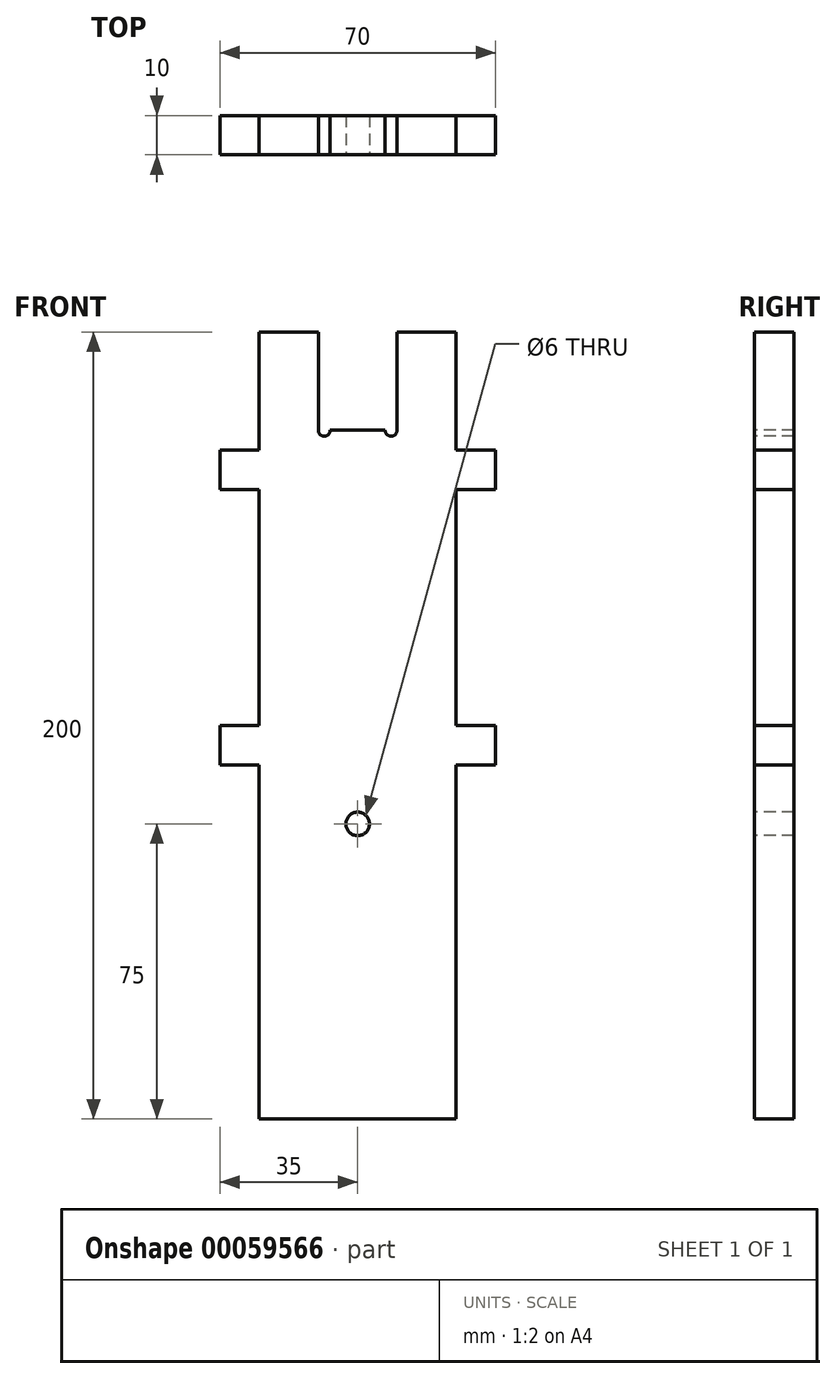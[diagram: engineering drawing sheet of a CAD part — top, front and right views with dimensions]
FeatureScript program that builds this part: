
annotation { "Feature Type Name" : "Feature", "Feature Type Description" : "" }
export const myFeature = defineFeature(function(context is Context, id is Id, definition is map)
    precondition{}
    {
        {
            var Q0;
            Q0=qCreatedBy(makeId("Front.planeOp"),FACE);
            var sketch = newSketch(context, id + "F0", { "sketchPlane" : qUnion([Q0])});
            skLineSegment(sketch, "E0.bottom", {"start": v(-25, 100) * mm, "end": v(25, 100) * mm});
            skLineSegment(sketch, "E0.top", {"start": v(-25, -100) * mm, "end": v(25, -100) * mm});
            skLineSegment(sketch, "E0.left", {"start": v(-25, 100) * mm, "end": v(-25, -100) * mm});
            skLineSegment(sketch, "E0.right", {"start": v(25, 100) * mm, "end": v(25, -100) * mm});
            skPoint(sketch, "E0.middle", {"position": v(0, 0) * mm});
            skSolve(sketch);
        }
        {
            var Q0;
            Q0=qSketchRegion(id+"F0",true);
            extrude(context, id + "F1", {"entities" : qUnion([Q0]), "depth" : 10 * mm});
        }
        {
            var Q0;
            Q0=makeQuery(id+"F1.opExtrude","CAP_FACE",FACE,{"disambiguationData":[OSD([sQuery(id+"F0.wireOp",EDGE,"E0.bottom"),sQuery(id+"F0.wireOp",EDGE,"E0.top"),sQuery(id+"F0.wireOp",EDGE,"E0.left"),sQuery(id+"F0.wireOp",EDGE,"E0.right")])],"isStart":false});
            var sketch = newSketch(context, id + "F2", { "sketchPlane" : qUnion([Q0])});
            skCircle(sketch, "E1", {"center": v(0, -25) * mm, "radius": 3 * mm});
            skSolve(sketch);
        }
        {
            var Q0;
            Q0=qSketchRegion(id+"F2",true);
            extrude(context, id + "F3", {"entities" : qUnion([Q0]), "operationType" : NewBodyOperationType.REMOVE, "oppositeDirection" : true, "depth" : 25 * mm});
        }
        {
            var Q0;
            Q0=makeQuery(id+"F1.opExtrude","CAP_FACE",FACE,{"disambiguationData":[OSD([sQuery(id+"F0.wireOp",EDGE,"E0.bottom"),sQuery(id+"F0.wireOp",EDGE,"E0.top"),sQuery(id+"F0.wireOp",EDGE,"E0.left"),sQuery(id+"F0.wireOp",EDGE,"E0.right")])],"isStart":false});
            var sketch = newSketch(context, id + "F4", { "sketchPlane" : qUnion([Q0])});
            skLineSegment(sketch, "E2.bottom", {"start": v(-10, 105) * mm, "end": v(10, 105) * mm});
            skLineSegment(sketch, "E2.top", {"start": v(-7, 75) * mm, "end": v(7, 75) * mm});
            skLineSegment(sketch, "E2.left", {"start": v(-10, 105) * mm, "end": v(-10, 75) * mm});
            skLineSegment(sketch, "E2.right", {"start": v(10, 105) * mm, "end": v(10, 75) * mm});
            skPoint(sketch, "E2.middle", {"position": v(0, 90) * mm});
            skArc(sketch, "E3", {"start": v(-10, 75) * mm, "mid": v(-8.5, 73.5) * mm, "end": v(-7, 75) * mm});
            skLineSegment(sketch, "E4", {"start": v(0, 75) * mm, "end": v(0, 25.67) * mm, "construction": true});
            skArc(sketch, "E5.MirrorCS", {"start": v(10, 75) * mm, "mid": v(8.5, 73.5) * mm, "end": v(7, 75) * mm});
            skSolve(sketch);
        }
        {
            var Q0;
            Q0=qSketchRegion(id+"F4",true);
            extrude(context, id + "F5", {"entities" : qUnion([Q0]), "operationType" : NewBodyOperationType.REMOVE, "oppositeDirection" : true, "depth" : 25 * mm});
        }
        {
            var Q0;
            Q0=makeQuery(id+"F1.opExtrude","CAP_FACE",FACE,{"disambiguationData":[OSD([sQuery(id+"F0.wireOp",EDGE,"E0.bottom"),sQuery(id+"F0.wireOp",EDGE,"E0.top"),sQuery(id+"F0.wireOp",EDGE,"E0.left"),sQuery(id+"F0.wireOp",EDGE,"E0.right")])],"isStart":false});
            var sketch = newSketch(context, id + "F6", { "sketchPlane" : qUnion([Q0])});
            skLineSegment(sketch, "E6.bottom", {"start": v(-25, 70) * mm, "end": v(-35, 70) * mm});
            skLineSegment(sketch, "E6.top", {"start": v(-25, 60) * mm, "end": v(-35, 60) * mm});
            skLineSegment(sketch, "E6.left", {"start": v(-25, 70) * mm, "end": v(-25, 60) * mm});
            skLineSegment(sketch, "E6.right", {"start": v(-35, 70) * mm, "end": v(-35, 60) * mm});
            skLineSegment(sketch, "E7.MirrorCS", {"start": v(25, 70) * mm, "end": v(35, 70) * mm});
            skLineSegment(sketch, "E8.MirrorCS", {"start": v(35, 70) * mm, "end": v(35, 60) * mm});
            skLineSegment(sketch, "E9.MirrorCS", {"start": v(25, 70) * mm, "end": v(25, 60) * mm});
            skLineSegment(sketch, "E10.MirrorCS", {"start": v(25, 60) * mm, "end": v(35, 60) * mm});
            skLineSegment(sketch, "E11", {"start": v(-25, 30) * mm, "end": v(25, 30) * mm, "construction": true});
            skLineSegment(sketch, "E12.MirrorCS", {"start": v(-25, -10) * mm, "end": v(-35, -10) * mm});
            skLineSegment(sketch, "E13.MirrorCS", {"start": v(25, 0) * mm, "end": v(35, 0) * mm});
            skLineSegment(sketch, "E14.MirrorCS", {"start": v(25, -10) * mm, "end": v(35, -10) * mm});
            skLineSegment(sketch, "E15.MirrorCS", {"start": v(-25, -10) * mm, "end": v(-25, 0) * mm});
            skLineSegment(sketch, "E16.MirrorCS", {"start": v(35, -10) * mm, "end": v(35, 0) * mm});
            skLineSegment(sketch, "E17.MirrorCS", {"start": v(-25, 0) * mm, "end": v(-35, 0) * mm});
            skLineSegment(sketch, "E18.MirrorCS", {"start": v(25, -10) * mm, "end": v(25, 0) * mm});
            skLineSegment(sketch, "E19.MirrorCS", {"start": v(-35, -10) * mm, "end": v(-35, 0) * mm});
            skSolve(sketch);
        }
        {
            var Q0;
            Q0=qSketchRegion(id+"F6",true);
            extrude(context, id + "F7", {"entities" : qUnion([Q0]), "operationType" : NewBodyOperationType.ADD, "oppositeDirection" : true, "depth" : 10 * mm});
        }
    });
